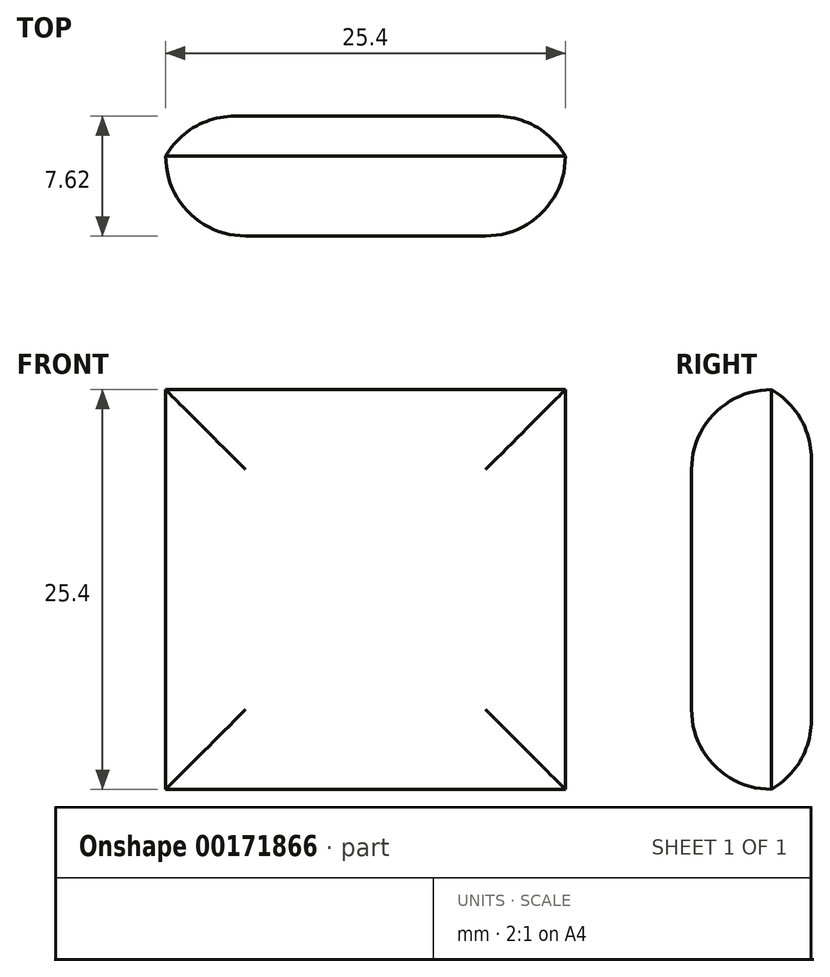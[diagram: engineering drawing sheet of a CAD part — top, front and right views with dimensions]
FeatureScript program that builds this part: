
annotation { "Feature Type Name" : "Feature", "Feature Type Description" : "" }
export const myFeature = defineFeature(function(context is Context, id is Id, definition is map)
    precondition{}
    {
        {
            var Q0;
            Q0=qCreatedBy(makeId("Front.planeOp"),FACE);
            var sketch = newSketch(context, id + "F0", { "sketchPlane" : qUnion([Q0])});
            skLineSegment(sketch, "E0.bottom", {"start": v(12.7, 12.7) * mm, "end": v(-12.7, 12.7) * mm});
            skLineSegment(sketch, "E0.top", {"start": v(12.7, -12.7) * mm, "end": v(-12.7, -12.7) * mm});
            skLineSegment(sketch, "E0.left", {"start": v(12.7, 12.7) * mm, "end": v(12.7, -12.7) * mm});
            skLineSegment(sketch, "E0.right", {"start": v(-12.7, 12.7) * mm, "end": v(-12.7, -12.7) * mm});
            skPoint(sketch, "E0.middle", {"position": v(0, 0) * mm});
            skSolve(sketch);
        }
        {
            var Q0;
            Q0=makeQuery(id+"F0.imprint","IMPRINT",FACE,{"disambiguationData":[TD([[makeQuery(id+"F0.imprint","IMPRINT",EDGE,{"derivedFrom":sQuery(id+"F0.wireOp",EDGE,"E0.bottom")}),1.0]])]});
            extrude(context, id + "F1", {"entities" : qUnion([Q0]), "depth" : 7.62 * mm});
        }
        {
            var Q0;
            Q0=makeQuery(id+"F1.opExtrude","CAP_EDGE",EDGE,{"disambiguationData":[OSD([sQuery(id+"F0.wireOp",EDGE,"E0.bottom")])],"isStart":false});
            var Q1;
            Q1=makeQuery(id+"F1.opExtrude","CAP_EDGE",EDGE,{"disambiguationData":[OSD([sQuery(id+"F0.wireOp",EDGE,"E0.right")])],"isStart":false});
            var Q2;
            Q2=makeQuery(id+"F1.opExtrude","CAP_EDGE",EDGE,{"disambiguationData":[OSD([sQuery(id+"F0.wireOp",EDGE,"E0.left")])],"isStart":false});
            var Q3;
            Q3=makeQuery(id+"F1.opExtrude","CAP_EDGE",EDGE,{"disambiguationData":[OSD([sQuery(id+"F0.wireOp",EDGE,"E0.top")])],"isStart":false});
            fillet(context, id + "F2", {"entities" : qUnion([Q0, Q1, Q2, Q3]), "radius" : 5.08 * mm, "tangentPropagation" : true, "allowEdgeOverflow" : false});
        }
        {
            var Q0;
            Q0=makeQuery(id+"F1.opExtrude","CAP_EDGE",EDGE,{"disambiguationData":[OSD([sQuery(id+"F0.wireOp",EDGE,"E0.top")])],"isStart":true});
            var Q1;
            Q1=makeQuery(id+"F1.opExtrude","CAP_EDGE",EDGE,{"disambiguationData":[OSD([sQuery(id+"F0.wireOp",EDGE,"E0.right")])],"isStart":true});
            var Q2;
            Q2=makeQuery(id+"F1.opExtrude","CAP_EDGE",EDGE,{"disambiguationData":[OSD([sQuery(id+"F0.wireOp",EDGE,"E0.left")])],"isStart":true});
            var Q3;
            Q3=makeQuery(id+"F1.opExtrude","CAP_EDGE",EDGE,{"disambiguationData":[OSD([sQuery(id+"F0.wireOp",EDGE,"E0.bottom")])],"isStart":true});
            fillet(context, id + "F3", {"entities" : qUnion([Q0, Q1, Q2, Q3]), "radius" : 5.08 * mm, "tangentPropagation" : true, "allowEdgeOverflow" : false});
        }
    });
